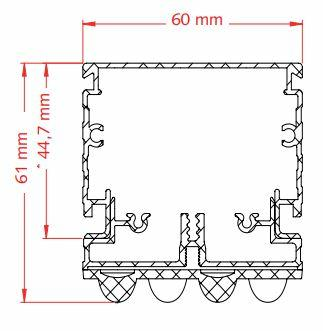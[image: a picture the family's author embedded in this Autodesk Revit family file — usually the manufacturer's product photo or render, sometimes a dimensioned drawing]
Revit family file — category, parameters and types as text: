
# Revit family: Rowan 2030mm
name_source: partatom
category: Lighting Fixtures
revit_build: Autodesk Revit 2017 (Build: 20190508_0315(x64)
units: mm (PartAtom-declared; Revit-internal decimal feet)

## family parameters
Always vertical = No
Cut with Voids When Loaded = No
Light Source = No
Part Type = Normal
Room Calculation Point = No
Round Connector Dimension = Use Diameter
Shared = No
Work Plane-Based = No

## types (3) — shared parameters
Article Number = On Request
Assembly Code = 63.0
Description = Veko Lightline
IK Value = IK02
IP Value = IP20
IfcExportAs = IfcLightFixtureType
IfcExportType = POINTSOURCE
Lamp = LED
Manufacturer = Veko Lightsystems
URL = https://www.veko.com
Wattage Comments = Load can vary between 10,3 - 154,5(W)

## per-type parameters (varying)
| type | Apparent Load | Model | Selected Optic |
| Narrow | 10 VA | Rowan Narrow | Optics Rowan 2030mm : Narrow |
| Semi Wide | 11 VA | Rowan Semi Wide | Optics Rowan 2030mm : Semi Wide |
| Wide | 11 VA | Rowan Wide | Optics Rowan 2030mm : Wide |

## geometry (parser evidence)
native form markers: Sweep x58
no freeform markers — native parametric forms only
